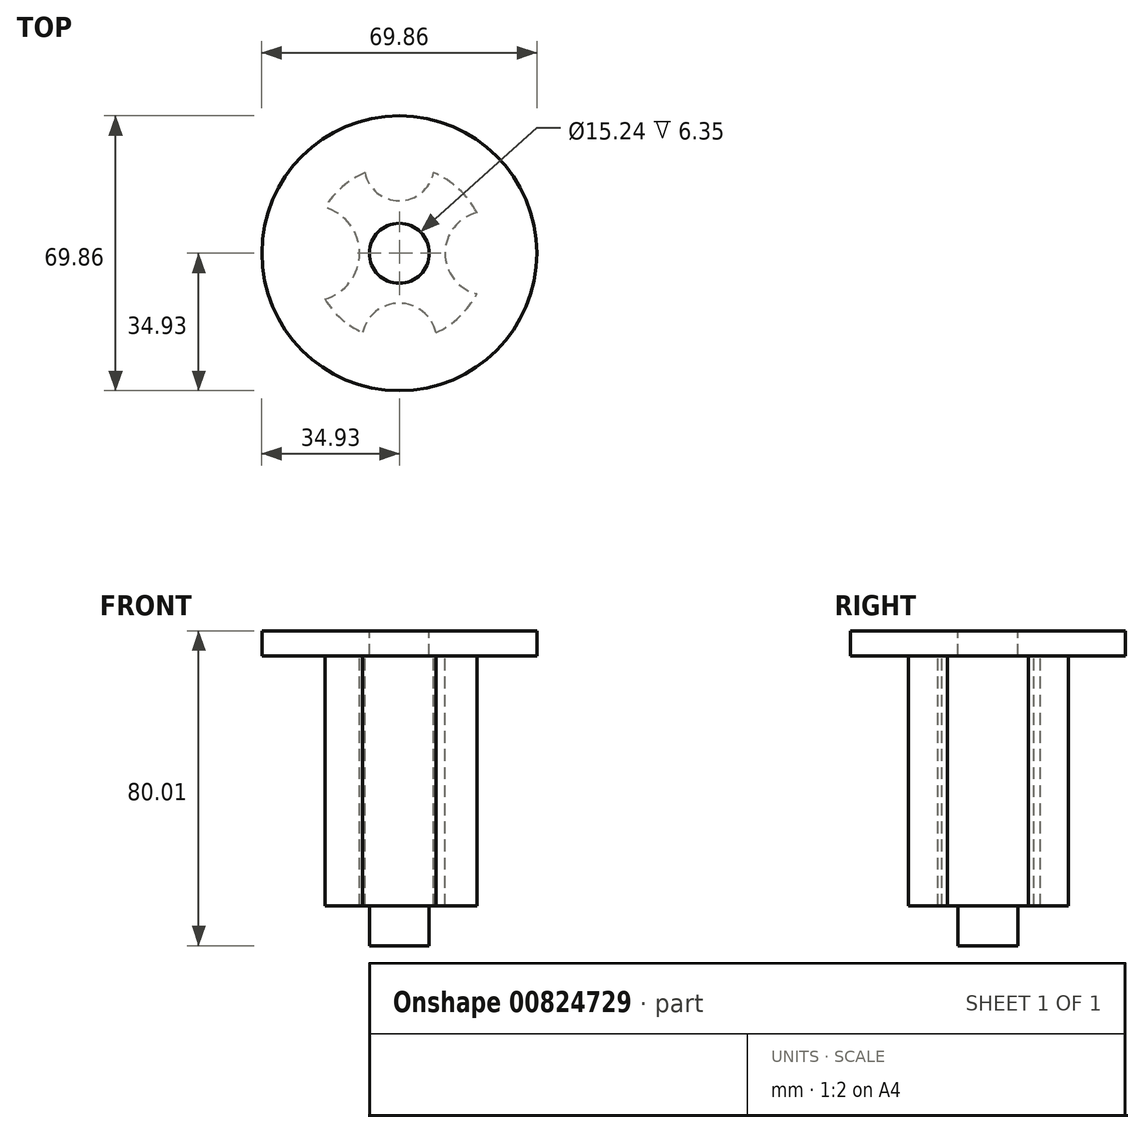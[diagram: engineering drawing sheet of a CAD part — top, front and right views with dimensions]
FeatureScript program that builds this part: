
annotation { "Feature Type Name" : "Feature", "Feature Type Description" : "" }
export const myFeature = defineFeature(function(context is Context, id is Id, definition is map)
    precondition{}
    {
        {
            var Q0;
            Q0=qCreatedBy(makeId("Top.planeOp"),FACE);
            var sketch = newSketch(context, id + "F0", { "sketchPlane" : qUnion([Q0])});
            skCircle(sketch, "E0", {"center": v(0, 0) * mm, "radius": 22.23 * mm});
            skCircle(sketch, "E1", {"center": v(-22.23, 0) * mm, "radius": 12.13 * mm});
            skCircle(sketch, "E2", {"center": v(0, 22.23) * mm, "radius": 8.9 * mm});
            skCircle(sketch, "E3", {"center": v(22.23, 0) * mm, "radius": 10.6 * mm});
            skCircle(sketch, "E4", {"center": v(0, -22.23) * mm, "radius": 9.53 * mm});
            skCircle(sketch, "E5", {"center": v(0, 0) * mm, "radius": 34.93 * mm});
            skCircle(sketch, "E6", {"center": v(0, 0) * mm, "radius": 7.62 * mm});
            skSolve(sketch);
        }
        {
            var Q0;
            {var subQ1=sQuery(id+"F0.wireOp",EDGE,"E0");var subQ8=sQuery(id+"F0.wireOp",EDGE,"E2");var subQ11=makeQuery(id+"F0.imprint","INTERSECT",VERTEX,{"disambiguationData":[OD(0.0)],"derivedFrom":[subQ1,subQ8]});Q0=makeQuery(id+"F0.imprint","IMPRINT",FACE,{"disambiguationData":[TD([[makeQuery(id+"F0.imprint","IMPRINT",EDGE,{"disambiguationData":[TD([[subQ11,1.0]])],"derivedFrom":subQ1}),1.0]])]});}
            extrude(context, id + "F1", {"entities" : qUnion([Q0]), "oppositeDirection" : true, "depth" : 63.5 * mm, "offsetDistance" : 25.4 * mm});
        }
        {
            var Q0;
            Q0=sQuery(id+"F0.wireOp",EDGE,"E5");
            extrude(context, id + "F2", {"bodyType" : ToolBodyType.SURFACE, "surfaceEntities" : qUnion([Q0]), "depth" : 6.35 * mm, "offsetDistance" : 25.4 * mm});
        }
        {
            var Q0;
            Q0=makeQuery(id+"F0.imprint","IMPRINT",FACE,{"disambiguationData":[TD([[makeQuery(id+"F0.imprint","IMPRINT",EDGE,{"derivedFrom":sQuery(id+"F0.wireOp",EDGE,"E5")}),1.0]])]});
            var Q1;
            {var subQ1=sQuery(id+"F0.wireOp",EDGE,"E0");var subQ8=sQuery(id+"F0.wireOp",EDGE,"E2");var subQ11=makeQuery(id+"F0.imprint","INTERSECT",VERTEX,{"disambiguationData":[OD(0.0)],"derivedFrom":[subQ1,subQ8]});Q1=makeQuery(id+"F0.imprint","IMPRINT",FACE,{"disambiguationData":[TD([[makeQuery(id+"F0.imprint","IMPRINT",EDGE,{"disambiguationData":[TD([[subQ11,1.0]])],"derivedFrom":subQ1}),1.0]])]});}
            var Q2;
            {var subQ0=sQuery(id+"F0.wireOp",EDGE,"E2");var subQ1=sQuery(id+"F0.wireOp",EDGE,"E0");var subQ2=makeQuery(id+"F0.imprint","INTERSECT",VERTEX,{"disambiguationData":[OD(0.0)],"derivedFrom":[subQ1,subQ0]});Q2=makeQuery(id+"F0.imprint","IMPRINT",FACE,{"disambiguationData":[TD([[makeQuery(id+"F0.imprint","IMPRINT",EDGE,{"disambiguationData":[TD([[subQ2,-1.0]])],"derivedFrom":subQ1}),1.0]])]});}
            var Q3;
            {var subQ0=sQuery(id+"F0.wireOp",EDGE,"E2");var subQ1=sQuery(id+"F0.wireOp",EDGE,"E0");var subQ2=makeQuery(id+"F0.imprint","INTERSECT",VERTEX,{"disambiguationData":[OD(0.0)],"derivedFrom":[subQ1,subQ0]});Q3=makeQuery(id+"F0.imprint","IMPRINT",FACE,{"disambiguationData":[TD([[makeQuery(id+"F0.imprint","IMPRINT",EDGE,{"disambiguationData":[TD([[subQ2,-1.0]])],"derivedFrom":subQ1}),-1.0]])]});}
            var Q4;
            {var subQ0=sQuery(id+"F0.wireOp",EDGE,"E3");var subQ1=sQuery(id+"F0.wireOp",EDGE,"E0");var subQ2=makeQuery(id+"F0.imprint","INTERSECT",VERTEX,{"disambiguationData":[OD(0.0)],"derivedFrom":[subQ1,subQ0]});Q4=makeQuery(id+"F0.imprint","IMPRINT",FACE,{"disambiguationData":[TD([[makeQuery(id+"F0.imprint","IMPRINT",EDGE,{"disambiguationData":[TD([[subQ2,1.0]])],"derivedFrom":subQ1}),1.0]])]});}
            var Q5;
            {var subQ0=sQuery(id+"F0.wireOp",EDGE,"E3");var subQ1=sQuery(id+"F0.wireOp",EDGE,"E0");var subQ2=makeQuery(id+"F0.imprint","INTERSECT",VERTEX,{"disambiguationData":[OD(0.0)],"derivedFrom":[subQ1,subQ0]});Q5=makeQuery(id+"F0.imprint","IMPRINT",FACE,{"disambiguationData":[TD([[makeQuery(id+"F0.imprint","IMPRINT",EDGE,{"disambiguationData":[TD([[subQ2,1.0]])],"derivedFrom":subQ1}),-1.0]])]});}
            var Q6;
            {var subQ0=sQuery(id+"F0.wireOp",EDGE,"E1");var subQ1=sQuery(id+"F0.wireOp",EDGE,"E0");var subQ2=makeQuery(id+"F0.imprint","INTERSECT",VERTEX,{"disambiguationData":[OD(0.0)],"derivedFrom":[subQ1,subQ0]});Q6=makeQuery(id+"F0.imprint","IMPRINT",FACE,{"disambiguationData":[TD([[makeQuery(id+"F0.imprint","IMPRINT",EDGE,{"disambiguationData":[TD([[subQ2,-1.0]])],"derivedFrom":subQ1}),-1.0]])]});}
            var Q7;
            {var subQ0=sQuery(id+"F0.wireOp",EDGE,"E1");var subQ1=sQuery(id+"F0.wireOp",EDGE,"E0");var subQ2=makeQuery(id+"F0.imprint","INTERSECT",VERTEX,{"disambiguationData":[OD(0.0)],"derivedFrom":[subQ1,subQ0]});Q7=makeQuery(id+"F0.imprint","IMPRINT",FACE,{"disambiguationData":[TD([[makeQuery(id+"F0.imprint","IMPRINT",EDGE,{"disambiguationData":[TD([[subQ2,-1.0]])],"derivedFrom":subQ1}),1.0]])]});}
            var Q8;
            {var subQ0=sQuery(id+"F0.wireOp",EDGE,"E4");var subQ1=sQuery(id+"F0.wireOp",EDGE,"E0");var subQ2=makeQuery(id+"F0.imprint","INTERSECT",VERTEX,{"disambiguationData":[OD(0.0)],"derivedFrom":[subQ1,subQ0]});Q8=makeQuery(id+"F0.imprint","IMPRINT",FACE,{"disambiguationData":[TD([[makeQuery(id+"F0.imprint","IMPRINT",EDGE,{"disambiguationData":[TD([[subQ2,-1.0]])],"derivedFrom":subQ1}),-1.0]])]});}
            var Q9;
            {var subQ0=sQuery(id+"F0.wireOp",EDGE,"E4");var subQ1=sQuery(id+"F0.wireOp",EDGE,"E0");var subQ2=makeQuery(id+"F0.imprint","INTERSECT",VERTEX,{"disambiguationData":[OD(0.0)],"derivedFrom":[subQ1,subQ0]});Q9=makeQuery(id+"F0.imprint","IMPRINT",FACE,{"disambiguationData":[TD([[makeQuery(id+"F0.imprint","IMPRINT",EDGE,{"disambiguationData":[TD([[subQ2,-1.0]])],"derivedFrom":subQ1}),1.0]])]});}
            extrude(context, id + "F3", {"entities" : qUnion([Q0, Q1, Q2, Q3, Q4, Q5, Q6, Q7, Q8, Q9]), "operationType" : NewBodyOperationType.ADD, "depth" : 6.35 * mm, "offsetDistance" : 25.4 * mm});
        }
        {
            var Q0;
            Q0=makeQuery(id+"F0.imprint","IMPRINT",FACE,{"disambiguationData":[TD([[makeQuery(id+"F0.imprint","IMPRINT",EDGE,{"derivedFrom":sQuery(id+"F0.wireOp",EDGE,"E6")}),1.0]])]});
            var Q1;
            Q1=sQuery(id+"F0.wireOp",EDGE,"E6");
            extrude(context, id + "F4", {"entities" : qUnion([Q0]), "operationType" : NewBodyOperationType.ADD, "surfaceOperationType" : NewSurfaceOperationType.ADD, "surfaceEntities" : qUnion([Q1]), "oppositeDirection" : true, "depth" : 73.66 * mm, "offsetDistance" : 25.4 * mm});
        }
    });
